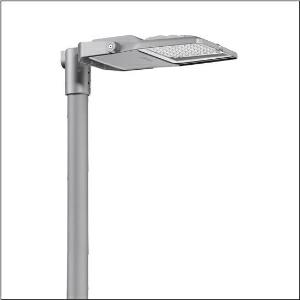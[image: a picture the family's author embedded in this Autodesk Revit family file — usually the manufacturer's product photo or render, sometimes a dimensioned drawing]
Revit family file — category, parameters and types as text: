
# Revit family: floodlight_fl_21_iq_mini___pl64_5xa7771c4e3a_84b6
name_source: partatom
category: Lighting Fixtures
units: mm (PartAtom-declared; Revit-internal decimal feet)

## family parameters
Cut with Voids When Loaded = No
Host = Face
Light Source = No
Part Type = Normal
Room Calculation Point = No
Round Connector Dimension = Use Diameter
Shared = No

## types (1)
- --- (1 x LED, 12280 lm, 87.2 W, 4000K)
    Apparent Load = 87 VA
    CIE Flux Codes = 28 80 98 100 100
    Color Rendering = 70
    Color Temperature = 4000K
    Default Elevation = 1800 mm
    Description = Floodlight FL 21 iQ mini, floodlight, primary light control with lens, of PMMA, primary optical cover: protective disc, of toughened safety glass, transparent, light distribution: PL64, light emission: direct distribution, installation type: surface-mounted, LED, High Power LED, rated luminous flux: 12.280lm, luminous efficacy: 141lm/W, light colour: 740, colour temperature: 4000K, control: Auto-Match, Temp-Guard, Lumen-Switch, Night-Set, Smart-Wire, Light-Fading, Desk-Remote (wireless, voltage-free reading and setting of iQ features in the workshop via application-optimized NFC function/RFID function), optimised constant luminous flux control (CLO 2.0), with terminal, 6-pole, mains connection: 220..240V, AC, 50/60Hz, start of lifetime: 87W, end of service life: 92W, reduction: 40W, luminaire housing, of diecast aluminium, powder-coated, Siteco® metallic grey (DB 702S), corrosivity category C5 mid according to DIN EN ISO 12944, sealing non-destructively replaceable, please order mast flange separately, mast bracket, of steel, galvanised, powder-coated, Siteco® metallic grey (DB 702S), protection rating (complete): IP66, insulation class (complete): insulation class II (safety insulation), certification: CE, ENEC, VDE, protection symbol: D, impact resistance: IK08, permissible operating ambient temperature: -40..+40°C, permissible operating ambient temperature for outdoor applications: -40..+50°C, standard: DIN EN 12944, LABS conformity tested according to VDMA 24364:2018-05, packaging unit: 1 piece

Light Distribution: PL64
    Height = 70 mm
    Lamp = 1 x LED
    Lamp Light Flux = 12280 lm
    Lamp Power = 87.2 W
    Lamp count = 1
    Length = 485 mm
    Luminous efficacy = 141 lm/W
    Manufacturer = Siteco
    ModVariant = No
    Model = 5XA7771C4E3A
    Number of Poles = 1
    OnlyDefault = Yes
    Power Factor = 1
    Product Name = Floodlight FL 21 iQ mini | PL64
    Product group = floodlight | pylon annexe
    ProductGroupID = 6200
    Protection Class = Protection class II
    Protection Degree = IP 66
    RLX_Detail_Level = 1
    RLX_Emergency_Light_Flux = 0 lm
    RLX_Emergency_Type = 0
    RLX_Emergency_Type_DB = No
    RlxData = <blob elided: 101381 chars, md5=fba8de7d>
    Socket = socket
    Standby Power = 0 W
    System Light Flux = 12280 lm
    System Power = 87 W
    Type Comments = factory setting: luminous flux: 100 % | dim-lin: 254 | 456 mA
    Type Image = l_1007125.jpg
    URL = http://relux.com
    VarID = @adj_116657
    Voltage = 0 V
    Weight = 0.00 kg
    Width = 337 mm

## geometry (parser evidence)
native form markers: Blend x4, Sweep x12
no freeform markers — native parametric forms only
